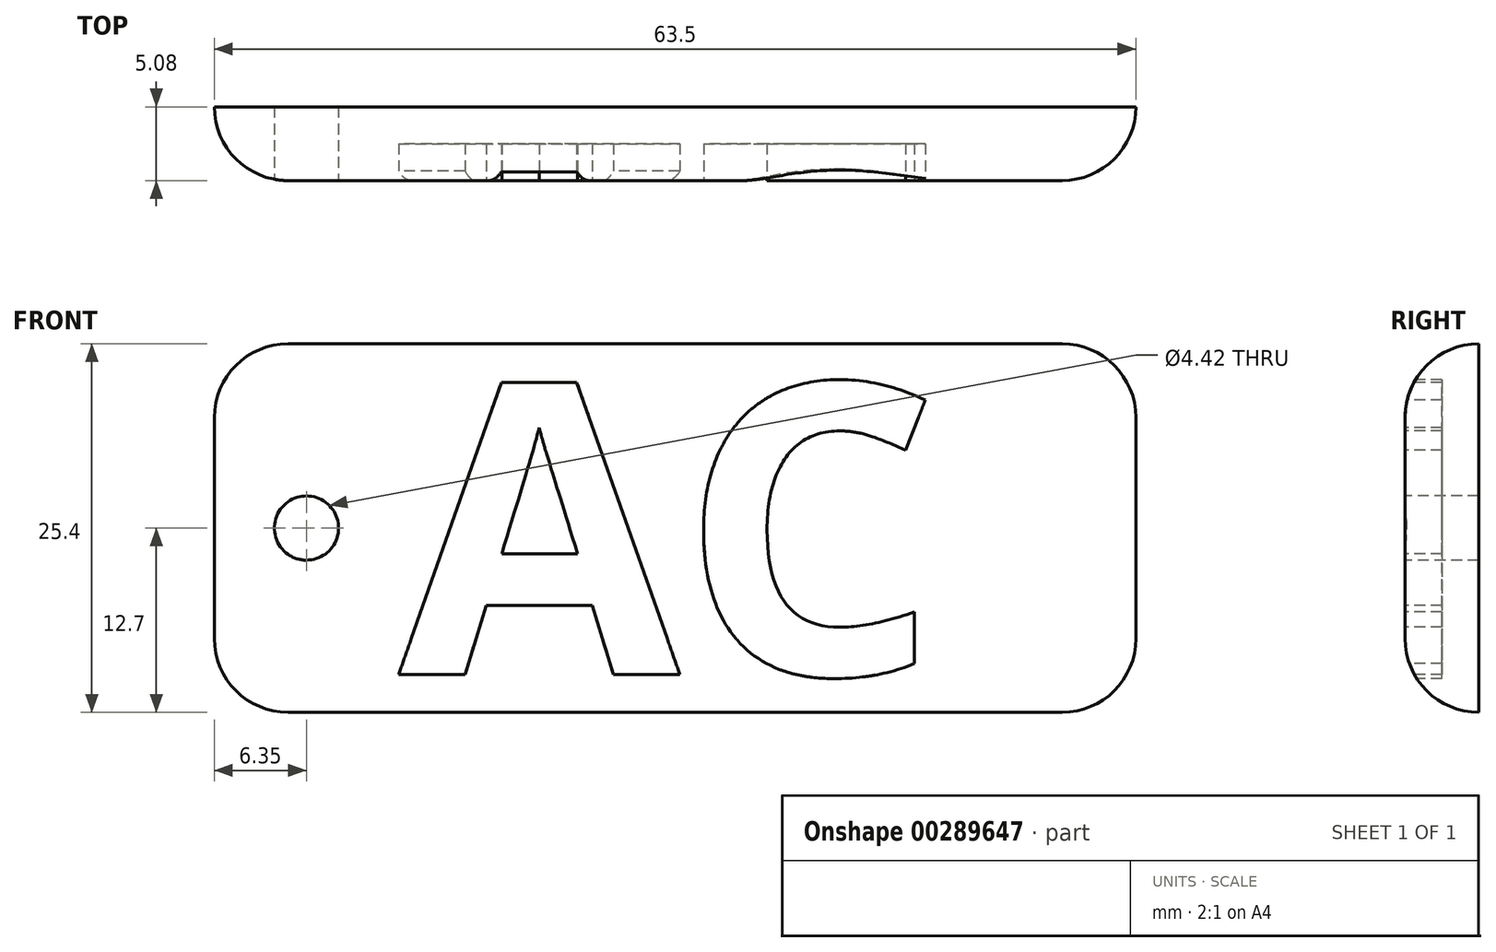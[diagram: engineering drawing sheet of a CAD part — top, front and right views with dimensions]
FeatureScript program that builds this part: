
annotation { "Feature Type Name" : "Feature", "Feature Type Description" : "" }
export const myFeature = defineFeature(function(context is Context, id is Id, definition is map)
    precondition{}
    {
        {
            var Q0;
            Q0=qCreatedBy(makeId("Front.planeOp"),FACE);
            var sketch = newSketch(context, id + "F0", { "sketchPlane" : qUnion([Q0])});
            skLineSegment(sketch, "E0.bottom", {"start": v(-31.75, 12.7) * mm, "end": v(31.75, 12.7) * mm});
            skLineSegment(sketch, "E0.top", {"start": v(-31.75, -12.7) * mm, "end": v(31.75, -12.7) * mm});
            skLineSegment(sketch, "E0.left", {"start": v(-31.75, 12.7) * mm, "end": v(-31.75, -12.7) * mm});
            skLineSegment(sketch, "E0.right", {"start": v(31.75, 12.7) * mm, "end": v(31.75, -12.7) * mm});
            skSolve(sketch);
        }
        {
            var Q0;
            Q0=makeQuery(id+"F0.imprint","IMPRINT",FACE,{"disambiguationData":[TD([[makeQuery(id+"F0.imprint","IMPRINT",EDGE,{"derivedFrom":sQuery(id+"F0.wireOp",EDGE,"E0.bottom")}),-1.0]])]});
            extrude(context, id + "F1", {"entities" : qUnion([Q0]), "depth" : 5.08 * mm});
        }
        {
            var Q0;
            Q0=makeQuery(id+"F1.opExtrude","SWEPT_EDGE",EDGE,{"disambiguationData":[OSD([sQuery(id+"F0.wireOp",EDGE,"E0.bottom"),sQuery(id+"F0.wireOp",EDGE,"E0.right")])]});
            var Q1;
            Q1=makeQuery(id+"F1.opExtrude","SWEPT_EDGE",EDGE,{"disambiguationData":[OSD([sQuery(id+"F0.wireOp",EDGE,"E0.top"),sQuery(id+"F0.wireOp",EDGE,"E0.right")])]});
            var Q2;
            Q2=makeQuery(id+"F1.opExtrude","SWEPT_EDGE",EDGE,{"disambiguationData":[OSD([sQuery(id+"F0.wireOp",EDGE,"E0.bottom"),sQuery(id+"F0.wireOp",EDGE,"E0.left")])]});
            var Q3;
            Q3=makeQuery(id+"F1.opExtrude","SWEPT_EDGE",EDGE,{"disambiguationData":[OSD([sQuery(id+"F0.wireOp",EDGE,"E0.top"),sQuery(id+"F0.wireOp",EDGE,"E0.left")])]});
            fillet(context, id + "F2", {"entities" : qUnion([Q0, Q1, Q2, Q3]), "radius" : 5.08 * mm, "tangentPropagation" : true, "allowEdgeOverflow" : false});
        }
        {
            var Q0;
            Q0=makeQuery(id+"F1.opExtrude","CAP_FACE",FACE,{"disambiguationData":[OSD([sQuery(id+"F0.wireOp",EDGE,"E0.bottom"),sQuery(id+"F0.wireOp",EDGE,"E0.top"),sQuery(id+"F0.wireOp",EDGE,"E0.left"),sQuery(id+"F0.wireOp",EDGE,"E0.right")])],"isStart":false});
            var sketch = newSketch(context, id + "F3", { "sketchPlane" : qUnion([Q0])});
            skCircle(sketch, "E1", {"center": v(-25.4, 0) * mm, "radius": 2.21 * mm});
            skSolve(sketch);
        }
        {
            var Q0;
            Q0=makeQuery(id+"F3.imprint","IMPRINT",FACE,{"disambiguationData":[TD([[makeQuery(id+"F3.imprint","IMPRINT",EDGE,{"derivedFrom":sQuery(id+"F3.wireOp",EDGE,"E1")}),1.0]])]});
            extrude(context, id + "F4", {"entities" : qUnion([Q0]), "operationType" : NewBodyOperationType.REMOVE, "endBound" : BoundingType.THROUGH_ALL, "oppositeDirection" : true, "depth" : 10.16 * mm});
        }
        {
            var Q0;
            Q0=makeQuery(id+"F1.opExtrude","CAP_FACE",FACE,{"disambiguationData":[OSD([sQuery(id+"F0.wireOp",EDGE,"E0.bottom"),sQuery(id+"F0.wireOp",EDGE,"E0.top"),sQuery(id+"F0.wireOp",EDGE,"E0.left"),sQuery(id+"F0.wireOp",EDGE,"E0.right")])],"isStart":false});
            var sketch = newSketch(context, id + "F5", { "sketchPlane" : qUnion([Q0])});
            skText(sketch, "E2", { "text": "AC", "fontName": "OpenSans-Bold.ttf"});
            const initialGuessF5  = {"E2": [-0.01905, -0.0101, 1, 0, 0.02022]};
            skSetInitialGuess(sketch, initialGuessF5);
            skSolve(sketch);
        }
        {
            var Q0;
            Q0=makeQuery(id+"F5.imprint","IMPRINT",FACE,{"disambiguationData":[TD([[makeQuery(id+"F5.imprint","IMPRINT",EDGE,{"derivedFrom":sQuery(id+"F5.wireOp",EDGE,"E2.sketch_text.stroke-0")}),-1.0]])]});
            var Q1;
            Q1=makeQuery(id+"F5.imprint","IMPRINT",FACE,{"disambiguationData":[TD([[makeQuery(id+"F5.imprint","IMPRINT",EDGE,{"derivedFrom":sQuery(id+"F5.wireOp",EDGE,"E2.sketch_text.stroke-12")}),-1.0]])]});
            extrude(context, id + "F6", {"entities" : qUnion([Q0, Q1]), "operationType" : NewBodyOperationType.REMOVE, "oppositeDirection" : true, "depth" : 2.54 * mm});
        }
        {
            var Q0;
            Q0=makeQuery(id+"F1.opExtrude","CAP_EDGE",EDGE,{"disambiguationData":[OSD([sQuery(id+"F0.wireOp",EDGE,"E0.right")])],"isStart":false});
            fillet(context, id + "F7", {"entities" : qUnion([Q0]), "radius" : 5.08 * mm, "tangentPropagation" : true, "allowEdgeOverflow" : false});
        }
    });
